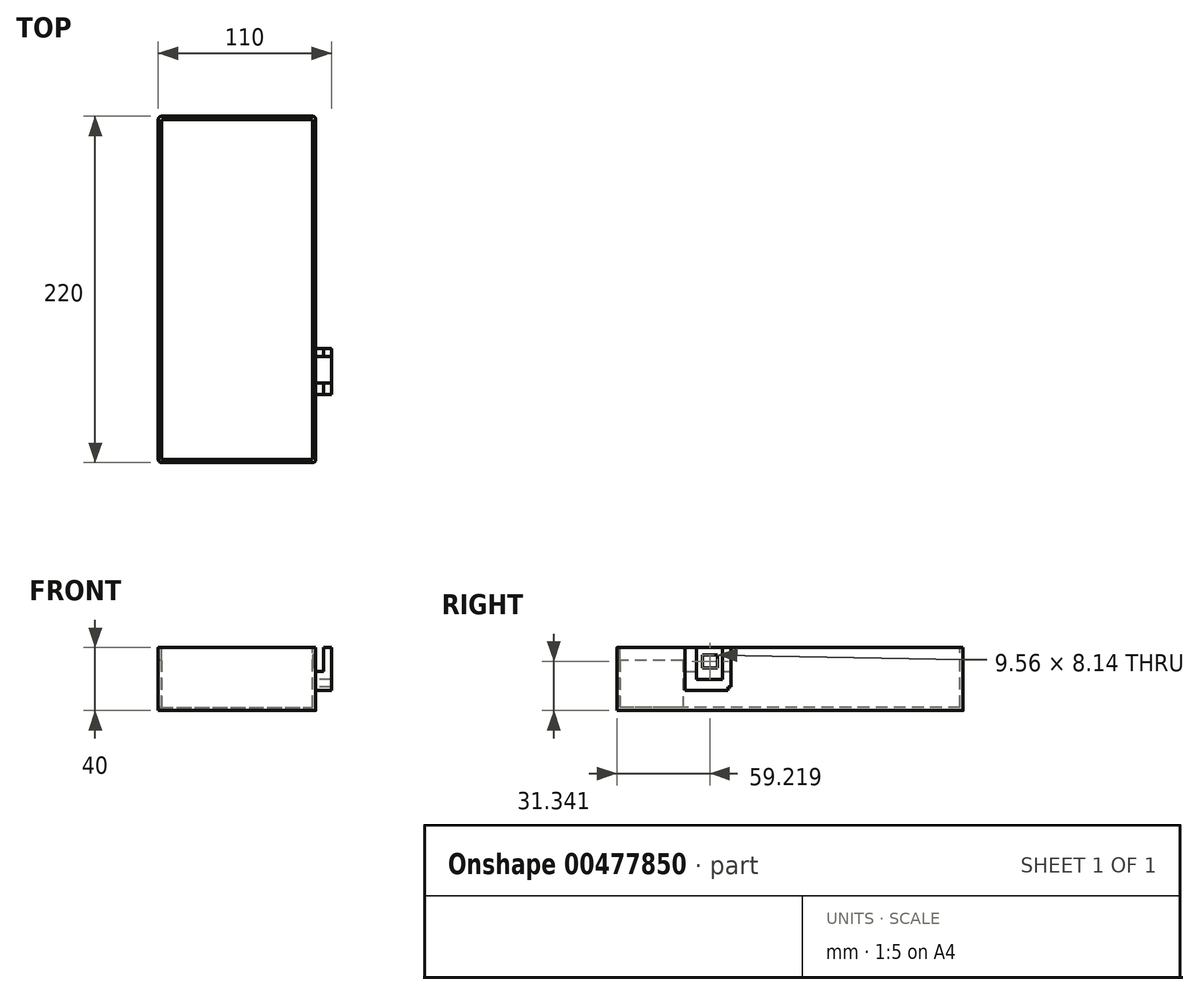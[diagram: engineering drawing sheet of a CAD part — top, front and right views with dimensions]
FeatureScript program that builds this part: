
annotation { "Feature Type Name" : "Feature", "Feature Type Description" : "" }
export const myFeature = defineFeature(function(context is Context, id is Id, definition is map)
    precondition{}
    {
        {
            var Q0;
            Q0=qCreatedBy(makeId("Top.planeOp"),FACE);
            var sketch = newSketch(context, id + "F0", { "sketchPlane" : qUnion([Q0])});
            skLineSegment(sketch, "E0.bottom", {"start": v(-53.3, 143.4) * mm, "end": v(46.7, 143.4) * mm});
            skLineSegment(sketch, "E0.top", {"start": v(-53.3, -76.6) * mm, "end": v(46.7, -76.6) * mm});
            skLineSegment(sketch, "E0.left", {"start": v(-53.3, 143.4) * mm, "end": v(-53.3, -76.6) * mm});
            skLineSegment(sketch, "E0.right", {"start": v(46.7, 143.4) * mm, "end": v(46.7, -76.6) * mm});
            skSolve(sketch);
        }
        {
            var Q0;
            Q0=makeQuery(id+"F0.imprint","IMPRINT",FACE,{"disambiguationData":[TD([[makeQuery(id+"F0.imprint","IMPRINT",EDGE,{"derivedFrom":sQuery(id+"F0.wireOp",EDGE,"E0.bottom")}),-1.0]])]});
            extrude(context, id + "F1", {"entities" : qUnion([Q0]), "depth" : 40 * mm});
        }
        {
            var Q0;
            Q0=makeQuery(id+"F1.opExtrude","CAP_FACE",FACE,{"disambiguationData":[OSD([sQuery(id+"F0.wireOp",EDGE,"E0.bottom"),sQuery(id+"F0.wireOp",EDGE,"E0.top"),sQuery(id+"F0.wireOp",EDGE,"E0.left"),sQuery(id+"F0.wireOp",EDGE,"E0.right")])],"isStart":false});
            var sketch = newSketch(context, id + "F2", { "sketchPlane" : qUnion([Q0])});
            skLineSegment(sketch, "E1.bottom", {"start": v(-51.3, 141.4) * mm, "end": v(44.7, 141.4) * mm});
            skLineSegment(sketch, "E1.top", {"start": v(-51.3, -74.6) * mm, "end": v(44.7, -74.6) * mm});
            skLineSegment(sketch, "E1.left", {"start": v(-51.3, 141.4) * mm, "end": v(-51.3, -74.6) * mm});
            skLineSegment(sketch, "E1.right", {"start": v(44.7, 141.4) * mm, "end": v(44.7, -74.6) * mm});
            skSolve(sketch);
        }
        {
            var Q0;
            Q0 = qSketchRegion(id + "F2", true);
            extrude(context, id + "F3", {"entities" : qUnion([Q0]), "operationType" : NewBodyOperationType.REMOVE, "oppositeDirection" : true, "depth" : 38 * mm});
        }
        {
            var Q0;
            Q0=makeQuery(id+"F1.opExtrude","SWEPT_FACE",FACE,{"disambiguationData":[OSD([sQuery(id+"F0.wireOp",EDGE,"E0.left")])]});
            var sketch = newSketch(context, id + "F4", { "sketchPlane" : qUnion([Q0])});
            skLineSegment(sketch, "E2.bottom", {"start": v(34.6, 32) * mm, "end": v(74.6, 32) * mm});
            skLineSegment(sketch, "E2.top", {"start": v(34.6, 2) * mm, "end": v(74.6, 2) * mm});
            skLineSegment(sketch, "E2.left", {"start": v(34.6, 32) * mm, "end": v(34.6, 2) * mm});
            skLineSegment(sketch, "E2.right", {"start": v(74.6, 32) * mm, "end": v(74.6, 2) * mm});
            skSolve(sketch);
        }
        {
            var Q0;
            Q0=makeQuery(id+"F1.opExtrude","SWEPT_EDGE",EDGE,{"disambiguationData":[OSD([sQuery(id+"F0.wireOp",EDGE,"E0.top"),sQuery(id+"F0.wireOp",EDGE,"E0.left")])]});
            var Q1;
            Q1=makeQuery(id+"F1.opExtrude","SWEPT_EDGE",EDGE,{"disambiguationData":[OSD([sQuery(id+"F0.wireOp",EDGE,"E0.top"),sQuery(id+"F0.wireOp",EDGE,"E0.right")])]});
            var Q2;
            Q2=makeQuery(id+"F1.opExtrude","SWEPT_EDGE",EDGE,{"disambiguationData":[OSD([sQuery(id+"F0.wireOp",EDGE,"E0.bottom"),sQuery(id+"F0.wireOp",EDGE,"E0.left")])]});
            var Q3;
            Q3=makeQuery(id+"F1.opExtrude","SWEPT_EDGE",EDGE,{"disambiguationData":[OSD([sQuery(id+"F0.wireOp",EDGE,"E0.bottom"),sQuery(id+"F0.wireOp",EDGE,"E0.right")])]});
            fillet(context, id + "F5", {"entities" : qUnion([Q0, Q1, Q2, Q3]), "radius" : 2 * mm, "tangentPropagation" : true, "allowEdgeOverflow" : false});
        }
        {
            var Q0;
            Q0 = qSketchRegion(id + "F4", true);
            extrude(context, id + "F6", {"entities" : qUnion([Q0]), "operationType" : NewBodyOperationType.REMOVE, "oppositeDirection" : true, "depth" : 2 * mm});
        }
        {
            var Q0;
            Q0=makeQuery(id+"F1.opExtrude","SWEPT_FACE",FACE,{"disambiguationData":[OSD([sQuery(id+"F0.wireOp",EDGE,"E0.right")])]});
            var sketch = newSketch(context, id + "F7", { "sketchPlane" : qUnion([Q0])});
            skLineSegment(sketch, "E3.bottom", {"start": v(141.4, 40) * mm, "end": v(33.4, 40) * mm});
            skLineSegment(sketch, "E3.top", {"start": v(141.4, 0) * mm, "end": v(33.4, 0) * mm});
            skLineSegment(sketch, "E3.left", {"start": v(141.4, 40) * mm, "end": v(141.4, 0) * mm});
            skLineSegment(sketch, "E3.right", {"start": v(33.4, 40) * mm, "end": v(33.4, 0) * mm});
            skLineSegment(sketch, "E4.bottom", {"start": v(35.4, 38) * mm, "end": v(139.4, 38) * mm});
            skLineSegment(sketch, "E4.top", {"start": v(35.4, 2) * mm, "end": v(139.4, 2) * mm});
            skLineSegment(sketch, "E4.left", {"start": v(35.4, 38) * mm, "end": v(35.4, 2) * mm});
            skLineSegment(sketch, "E4.right", {"start": v(139.4, 38) * mm, "end": v(139.4, 2) * mm});
            skSolve(sketch);
        }
        {
            var Q0;
            {var subQ0=sQuery(id+"F0.wireOp",EDGE,"E0.right");Q0=makeQuery(id+"FhgwXP0MCwaBPNj_1.boolean.opBoolean","SPLIT",FACE,{"disambiguationData":[TD([makeQuery(id+"FhgwXP0MCwaBPNj_1.opExtrude","SWEPT_FACE",FACE,{"disambiguationData":[OSD([sQuery(id+"F7.wireOp",EDGE,"E3.bottom")])]})])],"derivedFrom":makeQuery(id+"F1.opExtrude","SWEPT_FACE",FACE,{"disambiguationData":[OSD([subQ0])]})});}
            var sketch = newSketch(context, id + "F8", { "sketchPlane" : qUnion([Q0])});
            skLineSegment(sketch, "E5.bottom", {"start": v(-9.34, 40) * mm, "end": v(-4, 40) * mm});
            skLineSegment(sketch, "E5.top", {"start": v(-9.34, 14.9) * mm, "end": v(-4, 14.9) * mm});
            skLineSegment(sketch, "E5.left", {"start": v(-9.34, 40) * mm, "end": v(-9.34, 14.9) * mm});
            skLineSegment(sketch, "E5.right", {"start": v(-4, 40) * mm, "end": v(-4, 14.9) * mm});
            skSolve(sketch);
        }
        {
            var Q0;
            Q0 = qSketchRegion(id + "F8", true);
            extrude(context, id + "F9", {"entities" : qUnion([Q0]), "operationType" : NewBodyOperationType.ADD, "depth" : 10 * mm});
        }
        {
            var Q0;
            {var subQ0=sQuery(id+"F0.wireOp",EDGE,"E0.right");Q0=makeQuery(id+"FhgwXP0MCwaBPNj_1.boolean.opBoolean","SPLIT",FACE,{"disambiguationData":[TD([makeQuery(id+"FhgwXP0MCwaBPNj_1.opExtrude","SWEPT_FACE",FACE,{"disambiguationData":[OSD([sQuery(id+"F7.wireOp",EDGE,"E3.bottom")])]})])],"derivedFrom":makeQuery(id+"F1.opExtrude","SWEPT_FACE",FACE,{"disambiguationData":[OSD([subQ0])]})});}
            var sketch = newSketch(context, id + "F10", { "sketchPlane" : qUnion([Q0])});
            skLineSegment(sketch, "E6.bottom", {"start": v(-33.19, 40) * mm, "end": v(-25.9, 40) * mm});
            skLineSegment(sketch, "E6.top", {"start": v(-33.19, 12.73) * mm, "end": v(-25.9, 12.73) * mm});
            skLineSegment(sketch, "E6.left", {"start": v(-33.19, 40) * mm, "end": v(-33.19, 12.73) * mm});
            skLineSegment(sketch, "E6.right", {"start": v(-25.9, 40) * mm, "end": v(-25.9, 12.73) * mm});
            skSolve(sketch);
        }
        {
            var Q0;
            Q0 = qSketchRegion(id + "F10", true);
            extrude(context, id + "F11", {"entities" : qUnion([Q0]), "operationType" : NewBodyOperationType.ADD, "depth" : 10 * mm});
        }
        {
            var Q0;
            Q0=makeQuery(id+"F11.opExtrude","SWEPT_FACE",FACE,{"disambiguationData":[OSD([sQuery(id+"F10.wireOp",EDGE,"E6.right")])]});
            var sketch = newSketch(context, id + "F12", { "sketchPlane" : qUnion([Q0])});
            skLineSegment(sketch, "E7.bottom", {"start": v(-56.7, 12.73) * mm, "end": v(-46.7, 12.73) * mm});
            skLineSegment(sketch, "E7.top", {"start": v(-56.7, 19.85) * mm, "end": v(-46.7, 19.85) * mm});
            skLineSegment(sketch, "E7.left", {"start": v(-56.7, 12.73) * mm, "end": v(-56.7, 19.85) * mm});
            skLineSegment(sketch, "E7.right", {"start": v(-46.7, 12.73) * mm, "end": v(-46.7, 19.85) * mm});
            skSolve(sketch);
        }
        {
            var Q0;
            Q0 = qSketchRegion(id + "F12", true);
            extrude(context, id + "F13", {"entities" : qUnion([Q0]), "operationType" : NewBodyOperationType.ADD, "depth" : 19.9 * mm});
        }
        {
            var Q0;
            Q0=makeQuery(id+"F3.boolean.opBoolean","COPY",FACE,{"derivedFrom":makeQuery(id+"F3.opExtrude","SWEPT_FACE",FACE,{"disambiguationData":[OSD([sQuery(id+"F2.wireOp",EDGE,"E1.right")])]})});
            var sketch = newSketch(context, id + "F14", { "sketchPlane" : qUnion([Q0])});
            skLineSegment(sketch, "E8.bottom", {"start": v(12.6, 35.41) * mm, "end": v(22.16, 35.41) * mm});
            skLineSegment(sketch, "E8.top", {"start": v(12.6, 27.27) * mm, "end": v(22.16, 27.27) * mm});
            skLineSegment(sketch, "E8.left", {"start": v(12.6, 35.41) * mm, "end": v(12.6, 27.27) * mm});
            skLineSegment(sketch, "E8.right", {"start": v(22.16, 35.41) * mm, "end": v(22.16, 27.27) * mm});
            skSolve(sketch);
        }
        {
            var Q0;
            Q0 = qSketchRegion(id + "F14", true);
            extrude(context, id + "F15", {"entities" : qUnion([Q0]), "operationType" : NewBodyOperationType.REMOVE, "oppositeDirection" : true, "depth" : 25 * mm});
        }
        {
            var Q0;
            Q0=makeQuery(id+"F11.boolean.opBoolean","MERGE",FACE,{"derivedFrom":[makeQuery(id+"F9.boolean.opBoolean","MERGE",FACE,{"derivedFrom":[makeQuery(id+"F1.opExtrude","CAP_FACE",FACE,{"disambiguationData":[OSD([sQuery(id+"F0.wireOp",EDGE,"E0.bottom"),sQuery(id+"F0.wireOp",EDGE,"E0.top"),sQuery(id+"F0.wireOp",EDGE,"E0.left"),sQuery(id+"F0.wireOp",EDGE,"E0.right")])],"isStart":false}),makeQuery(id+"F9.opExtrude","SWEPT_FACE",FACE,{"disambiguationData":[OSD([sQuery(id+"F8.wireOp",EDGE,"E5.bottom")])]})]}),makeQuery(id+"F11.opExtrude","SWEPT_FACE",FACE,{"disambiguationData":[OSD([sQuery(id+"F10.wireOp",EDGE,"E6.bottom")])]})]});
            var sketch = newSketch(context, id + "F16", { "sketchPlane" : qUnion([Q0])});
            skLineSegment(sketch, "E9.bottom", {"start": v(51.7, -33.19) * mm, "end": v(46.7, -33.19) * mm});
            skLineSegment(sketch, "E9.top", {"start": v(51.7, -4) * mm, "end": v(46.7, -4) * mm});
            skLineSegment(sketch, "E9.left", {"start": v(51.7, -33.19) * mm, "end": v(51.7, -4) * mm});
            skLineSegment(sketch, "E9.right", {"start": v(46.7, -33.19) * mm, "end": v(46.7, -4) * mm});
            skSolve(sketch);
        }
        {
            var Q0;
            {var subQ0=sQuery(id+"F16.wireOp",EDGE,"E9.bottom");Q0=makeQuery(id+"F16.imprint","IMPRINT",FACE,{"disambiguationData":[TD([[makeQuery(id+"F16.imprint","IMPRINT",EDGE,{"derivedFrom":subQ0}),-1.0]])]});}
            var Q1;
            {var subQ0=sQuery(id+"F16.wireOp",EDGE,"E9.top");Q1=makeQuery(id+"F16.imprint","IMPRINT",FACE,{"disambiguationData":[TD([[makeQuery(id+"F16.imprint","IMPRINT",EDGE,{"derivedFrom":subQ0}),1.0]])]});}
            extrude(context, id + "F17", {"entities" : qUnion([Q0, Q1]), "operationType" : NewBodyOperationType.REMOVE, "oppositeDirection" : true, "depth" : 15 * mm});
        }
    });
